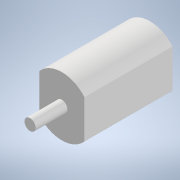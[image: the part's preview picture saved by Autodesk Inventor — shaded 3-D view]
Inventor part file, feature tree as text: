
AUTODESK INVENTOR PART (.ipt)
format: ipt  version: 2022 (Build 260153000, 153)  size: 102,912 bytes
history: native  units: mm
features: extrude x2, sketch x2
ambient origin geometry x8: Origin, YZ Plane, XZ Plane, XY Plane, X Axis, Y Axis, Z Axis, Center Point
bodies: Solid1 (feature_tree)
feature tree (4):
  extrude  "Extrusion1"  Depth=9.25mm
  extrude  "Extrusion2"  Depth=13.0mm
  sketch  "Sketch1"  dims[d0=24.2mm d1=9.25mm]
  sketch  "Sketch2"  dims[d2=36.0mm d3=0.0mm d4=4.6mm d5=13.0mm d6=0.0mm]
